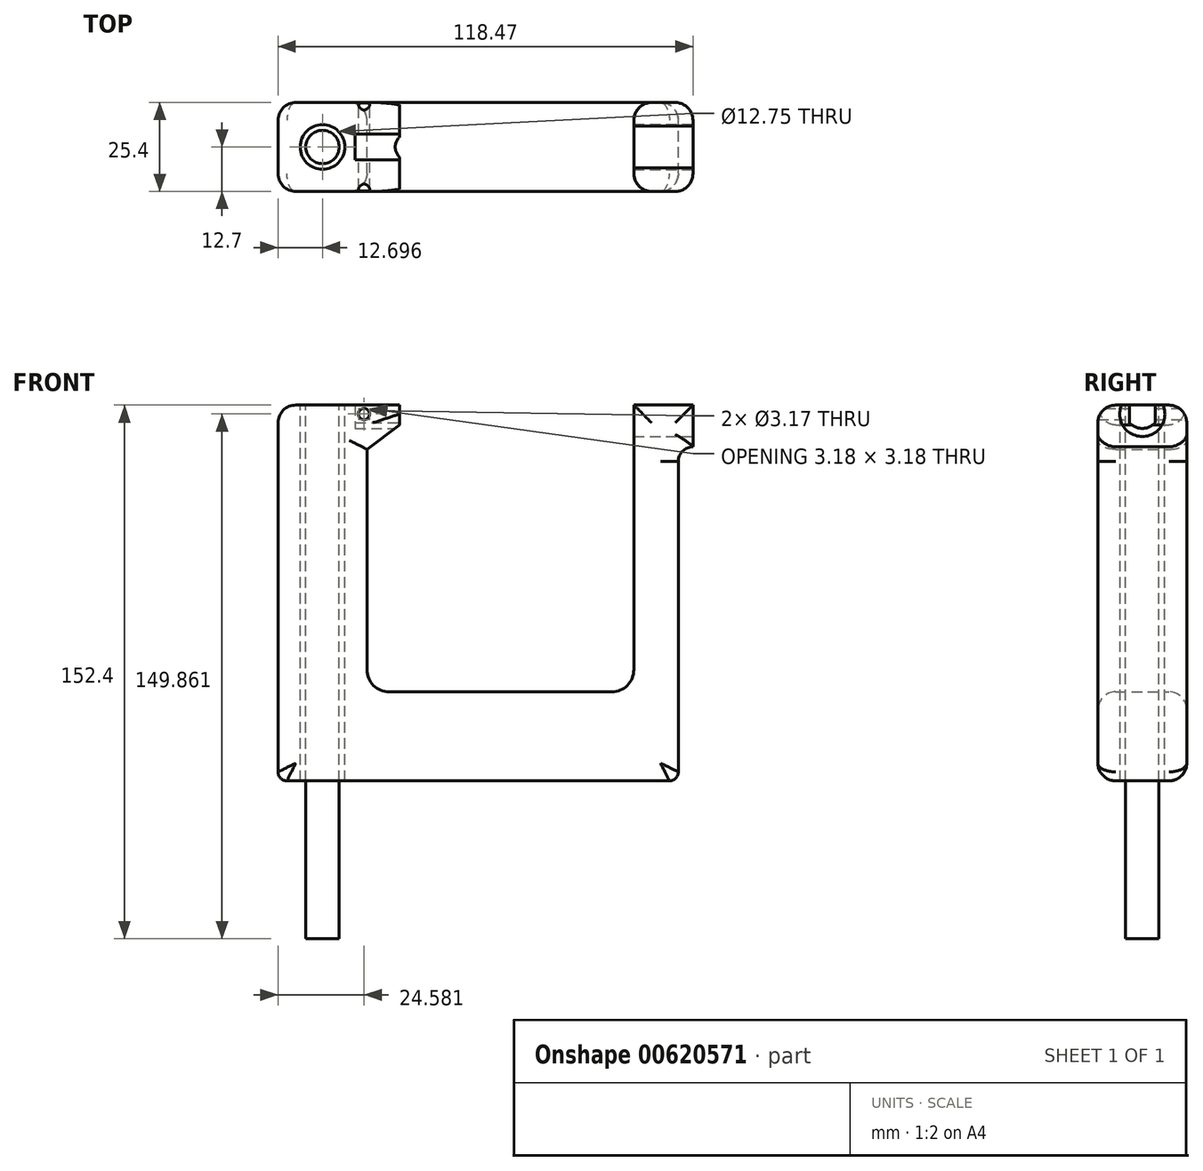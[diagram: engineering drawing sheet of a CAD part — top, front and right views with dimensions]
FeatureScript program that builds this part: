
annotation { "Feature Type Name" : "Feature", "Feature Type Description" : "" }
export const myFeature = defineFeature(function(context is Context, id is Id, definition is map)
    precondition{}
    {
        {
            var Q0;
            Q0=qCreatedBy(makeId("Front.planeOp"),FACE);
            var sketch = newSketch(context, id + "F0", { "sketchPlane" : qUnion([Q0])});
            skLineSegment(sketch, "E0.top", {"start": v(-47.46, -62.83) * mm, "end": v(-24.6, -62.83) * mm});
            skLineSegment(sketch, "E0.left", {"start": v(-50, 36.23) * mm, "end": v(-50, -60.29) * mm});
            skLineSegment(sketch, "E0.right", {"start": v(-24.6, 31.83) * mm, "end": v(-24.6, -31.08) * mm});
            skLineSegment(sketch, "E1.bottom", {"start": v(-24.6, -62.83) * mm, "end": v(61.76, -62.83) * mm});
            skLineSegment(sketch, "E1.top", {"start": v(-18.25, -37.43) * mm, "end": v(45.25, -37.43) * mm});
            skLineSegment(sketch, "E1.right", {"start": v(64.3, -60.29) * mm, "end": v(64.3, -37.43) * mm});
            skLineSegment(sketch, "E2.top", {"start": v(61.76, 44.46) * mm, "end": v(54.14, 44.46) * mm});
            skLineSegment(sketch, "E2.left", {"start": v(64.3, -37.43) * mm, "end": v(64.3, 28.4) * mm});
            skLineSegment(sketch, "E2.right", {"start": v(51.6, -31.08) * mm, "end": v(51.6, 41.92) * mm});
            skPoint(sketch, "E3.visualSharp", {"position": v(-50, -62.83) * mm});
            skArc(sketch, "E3.filletArc", {"start": v(-50, -60.29) * mm, "mid": v(-49.26, -62.08) * mm, "end": v(-47.46, -62.83) * mm});
            skPoint(sketch, "E4.visualSharp", {"position": v(64.3, -62.83) * mm});
            skArc(sketch, "E4.filletArc", {"start": v(61.76, -62.83) * mm, "mid": v(63.55, -62.08) * mm, "end": v(64.3, -60.29) * mm});
            skPoint(sketch, "E5.visualSharp", {"position": v(64.3, 44.46) * mm});
            skPoint(sketch, "E6.visualSharp", {"position": v(51.6, 44.46) * mm});
            skPoint(sketch, "E7.visualSharp", {"position": v(51.6, -37.43) * mm});
            skArc(sketch, "E7.filletArc", {"start": v(45.25, -37.43) * mm, "mid": v(49.74, -35.57) * mm, "end": v(51.6, -31.08) * mm});
            skPoint(sketch, "E8.visualSharp", {"position": v(-24.6, -37.43) * mm});
            skArc(sketch, "E8.filletArc", {"start": v(-24.6, -31.08) * mm, "mid": v(-22.74, -35.57) * mm, "end": v(-18.25, -37.43) * mm});
            skLineSegment(sketch, "E9", {"start": v(-15.26, 38.77) * mm, "end": v(-24.6, 31.83) * mm});
            skLineSegment(sketch, "E10", {"start": v(-25.42, 44.46) * mm, "end": v(-50, 44.46) * mm});
            skLineSegment(sketch, "E11", {"start": v(-50, 44.46) * mm, "end": v(-50, 36.23) * mm});
            skLineSegment(sketch, "E12", {"start": v(-15.26, 38.77) * mm, "end": v(-15.26, 44.46) * mm});
            skLineSegment(sketch, "E13", {"start": v(-15.26, 44.46) * mm, "end": v(-25.42, 44.46) * mm});
            skLineSegment(sketch, "E14", {"start": v(-25.42, 44.46) * mm, "end": v(-25.42, 41.92) * mm, "construction": true});
            skPoint(sketch, "E15", {"position": v(-25.42, 41.92) * mm});
            skLineSegment(sketch, "E16", {"start": v(61.76, 44.46) * mm, "end": v(64.3, 44.46) * mm});
            skLineSegment(sketch, "E17", {"start": v(51.6, 41.92) * mm, "end": v(51.6, 44.46) * mm});
            skLineSegment(sketch, "E18", {"start": v(54.14, 44.46) * mm, "end": v(51.6, 44.46) * mm});
            skLineSegment(sketch, "E19", {"start": v(64.3, 44.46) * mm, "end": v(68.47, 44.46) * mm});
            skLineSegment(sketch, "E20", {"start": v(68.47, 44.46) * mm, "end": v(68.47, 32.54) * mm});
            skPoint(sketch, "E21.orphan", {"position": v(64.3, 40.12) * mm});
            skArc(sketch, "E22", {"start": v(68.47, 32.54) * mm, "mid": v(65.5, 31.3) * mm, "end": v(64.3, 28.33) * mm});
            skSolve(sketch);
        }
        {
            var Q0;
            Q0 = qSketchRegion(id + "F0", true);
            extrude(context, id + "F1", {"entities" : qUnion([Q0]), "depth" : 25.4 * mm, "offsetDistance" : 25.4 * mm});
        }
        {
            var Q0;
            Q0=makeQuery(id+"F1.opExtrude","SWEPT_FACE",FACE,{"disambiguationData":[OSD([sQuery(id+"F0.wireOp",EDGE,"E12")])]});
            var sketch = newSketch(context, id + "F2", { "sketchPlane" : qUnion([Q0])});
            skLineSegment(sketch, "E23.bottom", {"start": v(-16.37, 44.46) * mm, "end": v(-9.03, 44.46) * mm});
            skLineSegment(sketch, "E23.left", {"start": v(-16.37, 44.46) * mm, "end": v(-16.37, 39.38) * mm});
            skLineSegment(sketch, "E23.right", {"start": v(-9.03, 44.46) * mm, "end": v(-9.03, 39.38) * mm});
            skLineSegment(sketch, "E24", {"start": v(-16.37, 44.46) * mm, "end": v(-9.03, 39.38) * mm, "construction": true});
            skLineSegment(sketch, "E25", {"start": v(-16.37, 39.38) * mm, "end": v(-9.03, 44.46) * mm, "construction": true});
            skPoint(sketch, "E26", {"position": v(-12.7, 41.92) * mm});
            skArc(sketch, "E27", {"start": v(-16.37, 39.38) * mm, "mid": v(-12.7, 37.81) * mm, "end": v(-9.03, 39.38) * mm});
            skSolve(sketch);
        }
        {
            var Q0;
            Q0 = qSketchRegion(id + "F2", true);
            extrude(context, id + "F3", {"entities" : qUnion([Q0]), "operationType" : NewBodyOperationType.REMOVE, "oppositeDirection" : true, "depth" : 12.7 * mm, "offsetDistance" : 25.4 * mm});
        }
        {
            var Q0;
            Q0=makeQuery(id+"F1.opExtrude","SWEPT_FACE",FACE,{"disambiguationData":[OSD([sQuery(id+"F0.wireOp",EDGE,"E0.left"),sQuery(id+"F0.wireOp",EDGE,"E11")])]});
            var Q1;
            Q1=makeQuery(id+"F1.opExtrude","CAP_FACE",FACE,{"disambiguationData":[OSD([sQuery(id+"F0.wireOp",EDGE,"E0.top"),sQuery(id+"F0.wireOp",EDGE,"E0.left"),sQuery(id+"F0.wireOp",EDGE,"E0.right"),sQuery(id+"F0.wireOp",EDGE,"E1.bottom"),sQuery(id+"F0.wireOp",EDGE,"E1.top"),sQuery(id+"F0.wireOp",EDGE,"E1.right"),sQuery(id+"F0.wireOp",EDGE,"E2.top"),sQuery(id+"F0.wireOp",EDGE,"E2.left"),sQuery(id+"F0.wireOp",EDGE,"E2.right"),sQuery(id+"F0.wireOp",EDGE,"E3.filletArc"),sQuery(id+"F0.wireOp",EDGE,"E4.filletArc"),sQuery(id+"F0.wireOp",EDGE,"E7.filletArc"),sQuery(id+"F0.wireOp",EDGE,"E8.filletArc"),sQuery(id+"F0.wireOp",EDGE,"E9"),sQuery(id+"F0.wireOp",EDGE,"E10"),sQuery(id+"F0.wireOp",EDGE,"E11"),sQuery(id+"F0.wireOp",EDGE,"E12"),sQuery(id+"F0.wireOp",EDGE,"E13"),sQuery(id+"F0.wireOp",EDGE,"E16"),sQuery(id+"F0.wireOp",EDGE,"E17"),sQuery(id+"F0.wireOp",EDGE,"E18"),sQuery(id+"F0.wireOp",EDGE,"E19"),sQuery(id+"F0.wireOp",EDGE,"E20"),sQuery(id+"F0.wireOp",EDGE,"B6KdYpWD-haeK-y5WO-W0zc-AOvqU7ZQ1LKf")])],"isStart":false});
            var Q2;
            Q2=makeQuery(id+"F1.opExtrude","CAP_FACE",FACE,{"disambiguationData":[OSD([sQuery(id+"F0.wireOp",EDGE,"E0.top"),sQuery(id+"F0.wireOp",EDGE,"E0.left"),sQuery(id+"F0.wireOp",EDGE,"E0.right"),sQuery(id+"F0.wireOp",EDGE,"E1.bottom"),sQuery(id+"F0.wireOp",EDGE,"E1.top"),sQuery(id+"F0.wireOp",EDGE,"E1.right"),sQuery(id+"F0.wireOp",EDGE,"E2.top"),sQuery(id+"F0.wireOp",EDGE,"E2.left"),sQuery(id+"F0.wireOp",EDGE,"E2.right"),sQuery(id+"F0.wireOp",EDGE,"E3.filletArc"),sQuery(id+"F0.wireOp",EDGE,"E4.filletArc"),sQuery(id+"F0.wireOp",EDGE,"E7.filletArc"),sQuery(id+"F0.wireOp",EDGE,"E8.filletArc"),sQuery(id+"F0.wireOp",EDGE,"E9"),sQuery(id+"F0.wireOp",EDGE,"E10"),sQuery(id+"F0.wireOp",EDGE,"E11"),sQuery(id+"F0.wireOp",EDGE,"E12"),sQuery(id+"F0.wireOp",EDGE,"E13"),sQuery(id+"F0.wireOp",EDGE,"E16"),sQuery(id+"F0.wireOp",EDGE,"E17"),sQuery(id+"F0.wireOp",EDGE,"E18"),sQuery(id+"F0.wireOp",EDGE,"E19"),sQuery(id+"F0.wireOp",EDGE,"E20"),sQuery(id+"F0.wireOp",EDGE,"B6KdYpWD-haeK-y5WO-W0zc-AOvqU7ZQ1LKf")])],"isStart":true});
            fillet(context, id + "F4", {"entities" : qUnion([Q0, Q1, Q2]), "radius" : 5.08 * mm, "tangentPropagation" : true, "allowEdgeOverflow" : false});
        }
        {
            var Q0;
            Q0=sQuery(id+"F0.wireOp",VERTEX,"E15");
            var Q1;
            Q1=makeQuery(id+"F1.opExtrude","SWEPT_BODY",BODY,{"disambiguationData":[OSD([sQuery(id+"F0.wireOp",EDGE,"E0.top"),sQuery(id+"F0.wireOp",EDGE,"E0.left"),sQuery(id+"F0.wireOp",EDGE,"E0.right"),sQuery(id+"F0.wireOp",EDGE,"E1.bottom"),sQuery(id+"F0.wireOp",EDGE,"E1.top"),sQuery(id+"F0.wireOp",EDGE,"E1.right"),sQuery(id+"F0.wireOp",EDGE,"E2.top"),sQuery(id+"F0.wireOp",EDGE,"E2.left"),sQuery(id+"F0.wireOp",EDGE,"E2.right"),sQuery(id+"F0.wireOp",EDGE,"E3.filletArc"),sQuery(id+"F0.wireOp",EDGE,"E4.filletArc"),sQuery(id+"F0.wireOp",EDGE,"E5.filletArc"),sQuery(id+"F0.wireOp",EDGE,"E6.filletArc"),sQuery(id+"F0.wireOp",EDGE,"E7.filletArc"),sQuery(id+"F0.wireOp",EDGE,"E8.filletArc"),sQuery(id+"F0.wireOp",EDGE,"E9"),sQuery(id+"F0.wireOp",EDGE,"E10"),sQuery(id+"F0.wireOp",EDGE,"E11"),sQuery(id+"F0.wireOp",EDGE,"E12"),sQuery(id+"F0.wireOp",EDGE,"E13")])]});
            hole(context, id + "F5", {"style" : HoleStyle.SIMPLE, "endStyle" : HoleEndStyle.THROUGH, "oppositeDirection" : true, "holeDiameter" : 3.17 * mm, "majorDiameter" : 6.35 * mm, "isTappedThrough" : true, "tappedDepth" : 12.7 * mm, "tapClearance" : 3, "locations" : qUnion([Q0]), "scope" : qUnion([Q1])});
        }
        {
            var Q0;
            Q0=makeQuery(id+"F1.opExtrude","SWEPT_FACE",FACE,{"disambiguationData":[OSD([sQuery(id+"F0.wireOp",EDGE,"E20")])]});
            var sketch = newSketch(context, id + "F6", { "sketchPlane" : qUnion([Q0])});
            skCircle(sketch, "E28", {"center": v(-12.7, 41.92) * mm, "radius": 6.45 * mm});
            skSolve(sketch);
        }
        {
            var Q0;
            Q0 = qSketchRegion(id + "F6", true);
            extrude(context, id + "F7", {"entities" : qUnion([Q0]), "operationType" : NewBodyOperationType.REMOVE, "oppositeDirection" : true, "depth" : 25.4 * mm, "offsetDistance" : 25.4 * mm, "hasSecondDirection" : true, "secondDirectionOppositeDirection" : false, "secondDirectionDepth" : 25.4 * mm});
        }
        {
            var Q0;
            Q0=makeQuery(id+"F1.opExtrude","SWEPT_FACE",FACE,{"disambiguationData":[OSD([sQuery(id+"F0.wireOp",EDGE,"E10"),sQuery(id+"F0.wireOp",EDGE,"E13")])]});
            var sketch = newSketch(context, id + "F8", { "sketchPlane" : qUnion([Q0])});
            skPoint(sketch, "E29", {"position": v(-37.3, -12.7) * mm});
            skCircle(sketch, "E30", {"center": v(-37.3, -12.7) * mm, "radius": 4.76 * mm});
            skSolve(sketch);
        }
        {
            var Q0;
            Q0=sQuery(id+"F8.wireOp",VERTEX,"E29");
            var Q1;
            Q1=makeQuery(id+"F1.opExtrude","SWEPT_BODY",BODY,{"disambiguationData":[OSD([sQuery(id+"F0.wireOp",EDGE,"E0.top"),sQuery(id+"F0.wireOp",EDGE,"E0.left"),sQuery(id+"F0.wireOp",EDGE,"E0.right"),sQuery(id+"F0.wireOp",EDGE,"E1.bottom"),sQuery(id+"F0.wireOp",EDGE,"E1.top"),sQuery(id+"F0.wireOp",EDGE,"E1.right"),sQuery(id+"F0.wireOp",EDGE,"E2.top"),sQuery(id+"F0.wireOp",EDGE,"E2.left"),sQuery(id+"F0.wireOp",EDGE,"E2.right"),sQuery(id+"F0.wireOp",EDGE,"E3.filletArc"),sQuery(id+"F0.wireOp",EDGE,"E4.filletArc"),sQuery(id+"F0.wireOp",EDGE,"E7.filletArc"),sQuery(id+"F0.wireOp",EDGE,"E8.filletArc"),sQuery(id+"F0.wireOp",EDGE,"E9"),sQuery(id+"F0.wireOp",EDGE,"E10"),sQuery(id+"F0.wireOp",EDGE,"E11"),sQuery(id+"F0.wireOp",EDGE,"E12"),sQuery(id+"F0.wireOp",EDGE,"E13"),sQuery(id+"F0.wireOp",EDGE,"E16"),sQuery(id+"F0.wireOp",EDGE,"E17"),sQuery(id+"F0.wireOp",EDGE,"E18"),sQuery(id+"F0.wireOp",EDGE,"E19"),sQuery(id+"F0.wireOp",EDGE,"E20"),sQuery(id+"F0.wireOp",EDGE,"E22")])]});
            hole(context, id + "F9", {"style" : HoleStyle.SIMPLE, "endStyle" : HoleEndStyle.THROUGH, "holeDiameter" : 12.75 * mm, "majorDiameter" : 6.35 * mm, "isTappedThrough" : true, "tappedDepth" : 12.7 * mm, "tapClearance" : 3, "startFromSketch" : true, "locations" : qUnion([Q0]), "scope" : qUnion([Q1])});
        }
        {
            var Q0;
            Q0 = qSketchRegion(id + "F8", true);
            var Q1;
            Q1=makeQuery(id+"F1.opExtrude","SWEPT_FACE",FACE,{"disambiguationData":[OSD([sQuery(id+"F0.wireOp",EDGE,"E0.top"),sQuery(id+"F0.wireOp",EDGE,"E1.bottom")])]});
            extrude(context, id + "F10", {"entities" : qUnion([Q0]), "oppositeDirection" : true, "depth" : 152.4 * mm, "endBoundEntityFace" : qUnion([Q1]), "offsetDistance" : 25.4 * mm});
        }
    });
